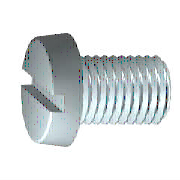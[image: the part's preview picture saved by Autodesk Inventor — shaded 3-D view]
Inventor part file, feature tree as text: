
AUTODESK INVENTOR PART (.ipt)
format: ipt  version: 2023 (Build 270158000, 158)  size: 182,272 bytes
history: native  units: mm (DEFAULTED — no unit token found)
features: sketch x2, extrude x1, plane x1
ambient origin geometry x7: Origin, YZ Plane, XZ Plane, X Axis, Y Axis, Z Axis, Center Point
bodies: Solid1 (feature_tree), Body (feature_tree)
feature tree (4):
  sketch  "Sketch2"  dims[d2=0.49086mm d3=3.3mm d4=5.0mm d5=4.566987mm d8=90.0deg d7=0.0mm d9=8.5mm d10=0.872665mm d11=1.2mm d12=8.5mm d14=0.2mm d15=20.4mm d16=0.0mm d17=0.433015mm d18=0.49086mm d19=1.3mm d20=0.0mm d36=45.0deg d37=0.0mm d39=0.0mm]
  extrude  "Slot"  Depth=20.4mm
  plane  "Work Plane1"
  sketch  "Sketch1"  dims[d0=22.0mm d1=20.4mm]
